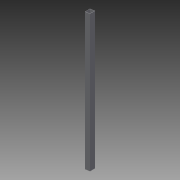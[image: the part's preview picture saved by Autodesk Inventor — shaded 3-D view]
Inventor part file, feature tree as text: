
AUTODESK INVENTOR PART (.ipt)
format: ipt  version: 2013 (Build 170138000, 138)  size: 88,064 bytes
history: native  units: in
note: dims shown in document units (in); Inventor stores cm internally (conversion verified against a paired STEP export)
features: extrude x2, sketch x2
ambient origin geometry x8: Origin, YZ Plane, XZ Plane, XY Plane, X Axis, Y Axis, Z Axis, Center Point
bodies: Solid1 (feature_tree)
feature tree (4):
  extrude  "Extrusion1"  Depth=1.0in
  extrude  "Extrusion2"  Depth=35.0in TaperAngle=0.0deg
  sketch  "Sketch1"  dims[d0=1.0in d2=1.0in]
  sketch  "Sketch2"  dims[d3=0.0625in d4=35.0in d5=0.0in d6=26.5in d8=35.0in d9=0.0in d10=26.7465in]
